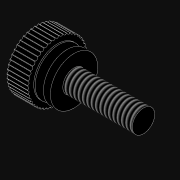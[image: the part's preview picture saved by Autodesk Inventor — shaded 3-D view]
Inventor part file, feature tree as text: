
AUTODESK INVENTOR PART (.ipt)
format: ipt  version: 2021.3 (Build 253353010, 353A)  size: 438,272 bytes
history: native  units: in
note: dims shown in document units (in); Inventor stores cm internally (conversion verified against a paired STEP export)
features: other x2, extrude x2, sketch x2, thread x1, pattern_circular x1, imported_body x1
ambient origin geometry x8: Origin, YZ Plane, XZ Plane, XY Plane, X Axis, Y Axis, Z Axis, Center Point
bodies: Body1 (feature_tree)
feature tree (9):
  parser-record x1  (decoder bookkeeping rows leaked as tree rows — omitted from the tree; the rows remain in map.json)
  other  "8-32 x 0.500'' Thumbscrew"
  thread  "Thread1"  [1 undecoded]
  extrude  "Extrusion1"  Depth=0.005in TaperAngle=0.0deg
  extrude  "Extrusion2"  Depth=0.0073in
  pattern_circular  "Circular Pattern1"  [2 undecoded]
  imported_body  "Base1"
  sketch  "Sketch1"  dims[d2=0.2135in d3=0.005in d4=0.0in]
  sketch  "Sketch2"  dims[d20=0.006in d21=0.0073in d22=0.0073in d23=0.006in d24=18.8976in d26=360.0deg d28=1.0in d29=0.0in d30=18.8976in d31=360.0deg d33=0.0in]
note: 3 required parameter values undecoded (feature->parameter linkage not recoverable at this tier; creation-order binding heuristic only, values carry confidence <= 0.55)
